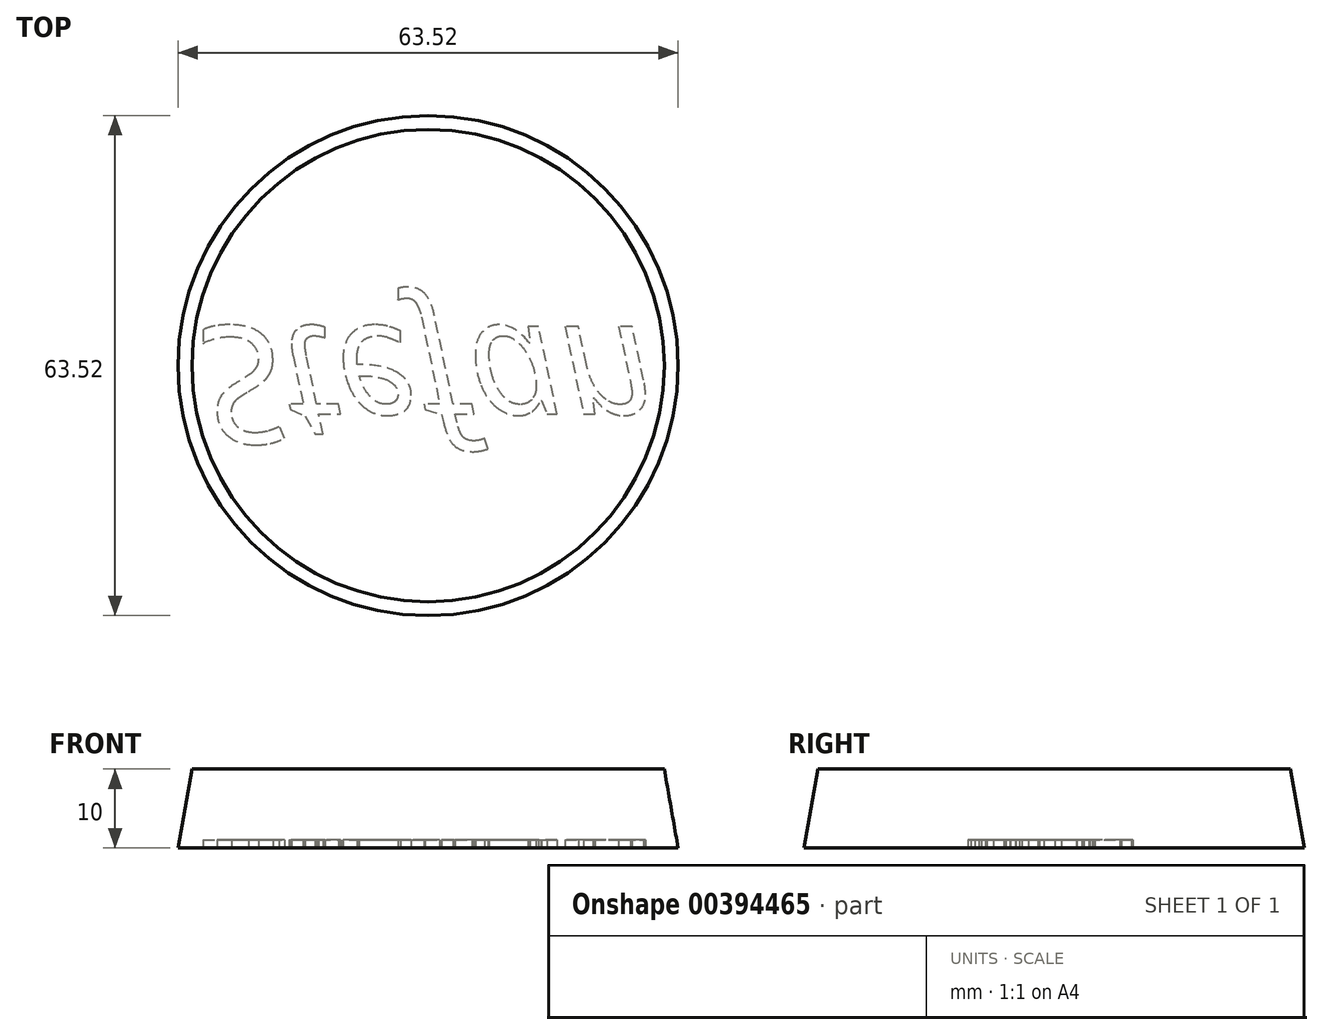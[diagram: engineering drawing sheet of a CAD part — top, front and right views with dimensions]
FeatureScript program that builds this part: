
annotation { "Feature Type Name" : "Feature", "Feature Type Description" : "" }
export const myFeature = defineFeature(function(context is Context, id is Id, definition is map)
    precondition{}
    {
        {
            var Q0;
            Q0=qCreatedBy(makeId("Top.planeOp"),FACE);
            var sketch = newSketch(context, id + "F0", { "sketchPlane" : qUnion([Q0])});
            skCircle(sketch, "E0", {"center": v(0, 0) * mm, "radius": 30 * mm});
            skSolve(sketch);
        }
        {
            var Q0;
            Q0=makeQuery(id+"F0.imprint","IMPRINT",FACE,{"disambiguationData":[TD([[makeQuery(id+"F0.imprint","IMPRINT",EDGE,{"derivedFrom":sQuery(id+"F0.wireOp",EDGE,"E0")}),1.0]])]});
            extrude(context, id + "F1", {"entities" : qUnion([Q0]), "oppositeDirection" : true, "depth" : 10 * mm, "hasDraft" : true, "draftAngle" : 10 * degree});
        }
        {
            var Q0;
            Q0=makeQuery(id+"F1.opExtrude","CAP_FACE",FACE,{"disambiguationData":[OSD([sQuery(id+"F0.wireOp",EDGE,"E0")])],"isStart":false});
            var sketch = newSketch(context, id + "F2", { "sketchPlane" : qUnion([Q0])});
            skText(sketch, "E1", { "text": "Stefan", "fontName": "OpenSans-Italic.ttf"});
            const initialGuessF2  = {"E1": [-0.029, -0.005, 1, 0, 0.015]};
            skSetInitialGuess(sketch, initialGuessF2);
            skSolve(sketch);
        }
        {
            var Q0;
            Q0=qSketchRegion(id+"F2",true);
            extrude(context, id + "F3", {"entities" : qUnion([Q0]), "operationType" : NewBodyOperationType.REMOVE, "oppositeDirection" : true, "depth" : 1 * mm});
        }
    });
